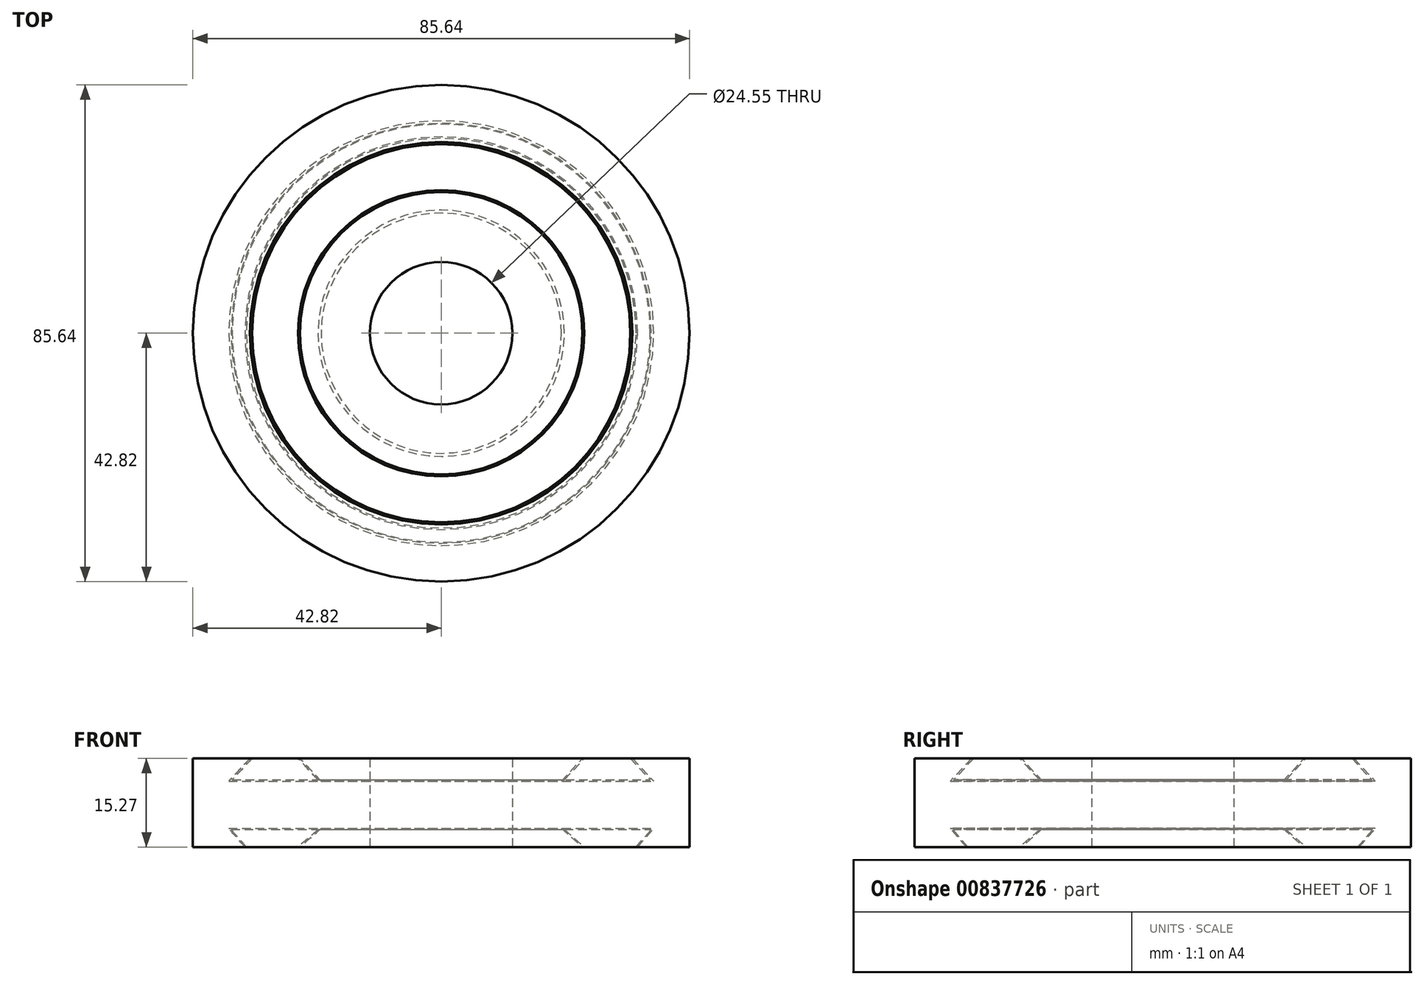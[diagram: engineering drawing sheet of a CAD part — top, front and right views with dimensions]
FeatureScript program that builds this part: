
annotation { "Feature Type Name" : "Feature", "Feature Type Description" : "" }
export const myFeature = defineFeature(function(context is Context, id is Id, definition is map)
    precondition{}
    {
        {
            var Q0;
            Q0=qCreatedBy(makeId("Right.planeOp"),FACE);
            var sketch = newSketch(context, id + "F0", { "sketchPlane" : qUnion([Q0])});
            skLineSegment(sketch, "E0", {"start": v(0, 0) * mm, "end": v(0, 17.61) * mm});
            skLineSegment(sketch, "E1", {"start": v(-42.82, 0) * mm, "end": v(-42.82, 15.27) * mm});
            skLineSegment(sketch, "E2", {"start": v(-42.82, 15.27) * mm, "end": v(-32.98, 15.27) * mm});
            skLineSegment(sketch, "E3", {"start": v(-32.98, 15.27) * mm, "end": v(-36.63, 11.34) * mm});
            skLineSegment(sketch, "E4", {"start": v(-36.63, 11.34) * mm, "end": v(-20.7, 11.34) * mm});
            skLineSegment(sketch, "E5", {"start": v(-20.7, 11.34) * mm, "end": v(-24.36, 15.27) * mm});
            skLineSegment(sketch, "E6", {"start": v(-24.36, 15.27) * mm, "end": v(-12.27, 15.27) * mm});
            skLineSegment(sketch, "E7", {"start": v(-12.27, 15.27) * mm, "end": v(-12.27, 0) * mm});
            skLineSegment(sketch, "E8", {"start": v(-12.27, 0) * mm, "end": v(-20.7, 0) * mm});
            skLineSegment(sketch, "E9", {"start": v(-20.7, 0) * mm, "end": v(-24.36, 0) * mm});
            skLineSegment(sketch, "E10", {"start": v(-24.36, 0) * mm, "end": v(-20.7, 3.19) * mm});
            skLineSegment(sketch, "E11", {"start": v(-20.7, 3.19) * mm, "end": v(-36.63, 3.19) * mm});
            skLineSegment(sketch, "E12", {"start": v(-36.63, 3.19) * mm, "end": v(-33.86, 0) * mm});
            skLineSegment(sketch, "E13", {"start": v(-33.86, 0) * mm, "end": v(-42.82, 0) * mm});
            skLineSegment(sketch, "E14", {"start": v(-32.81, 15.05) * mm, "end": v(-36.05, 11.57) * mm});
            skLineSegment(sketch, "E15", {"start": v(-36.05, 11.57) * mm, "end": v(-21.24, 11.57) * mm});
            skLineSegment(sketch, "E16", {"start": v(-21.24, 11.57) * mm, "end": v(-24.68, 15.27) * mm});
            skLineSegment(sketch, "E17", {"start": v(-32.81, 15.05) * mm, "end": v(-32.61, 15.27) * mm});
            skLineSegment(sketch, "E18", {"start": v(-32.61, 15.27) * mm, "end": v(-24.68, 15.27) * mm});
            skLineSegment(sketch, "E19", {"start": v(-24.68, 0) * mm, "end": v(-21.24, 3) * mm});
            skLineSegment(sketch, "E20", {"start": v(-21.24, 3) * mm, "end": v(-36.22, 3) * mm});
            skLineSegment(sketch, "E21", {"start": v(-36.22, 3) * mm, "end": v(-33.6, 0) * mm});
            skLineSegment(sketch, "E22", {"start": v(-33.6, 0) * mm, "end": v(-24.68, 0) * mm});
            skSolve(sketch);
        }
        {
            var Q0;
            Q0 = qSketchRegion(id + "F0", true);
            var Q1;
            Q1=sQuery(id+"F0.wireOp",EDGE,"E0");
            revolve(context, id + "F1", {"surfaceOperationType" : NewSurfaceOperationType.NEW, "entities" : qUnion([Q0]), "axis" : qUnion([Q1]), "revolveType" : RevolveType.FULL});
        }
    });
